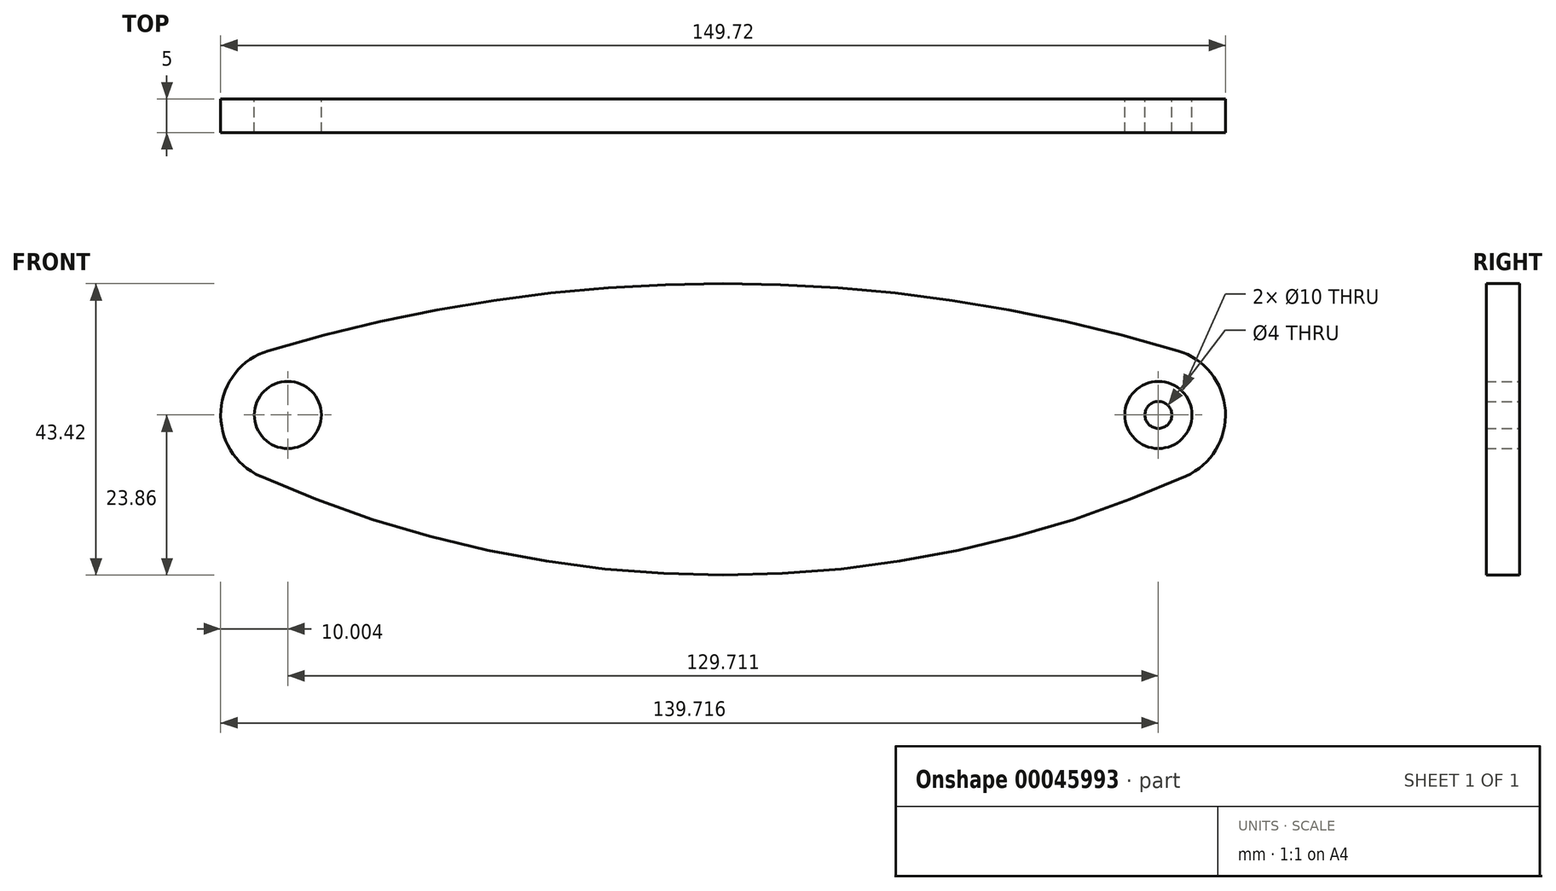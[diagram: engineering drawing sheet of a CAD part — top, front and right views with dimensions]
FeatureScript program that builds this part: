
annotation { "Feature Type Name" : "Feature", "Feature Type Description" : "" }
export const myFeature = defineFeature(function(context is Context, id is Id, definition is map)
    precondition{}
    {
        {
            var Q0;
            Q0=qCreatedBy(makeId("Front.planeOp"),FACE);
            var sketch = newSketch(context, id + "F0", { "sketchPlane" : qUnion([Q0])});
            skLineSegment(sketch, "E0", {"start": v(-64.86, 0) * mm, "end": v(64.86, 0) * mm, "construction": true});
            skCircle(sketch, "E1", {"center": v(-64.86, 0) * mm, "radius": 2 * mm});
            skCircle(sketch, "E2", {"center": v(64.86, 0) * mm, "radius": 2 * mm});
            skCircle(sketch, "E3", {"center": v(-64.86, 0) * mm, "radius": 5 * mm});
            skCircle(sketch, "E4", {"center": v(64.86, 0) * mm, "radius": 5 * mm});
            skArc(sketch, "E5", {"start": v(-68.94, -9.13) * mm, "mid": v(-74.83, 0.64) * mm, "end": v(-67.74, 9.57) * mm});
            skArc(sketch, "E6", {"start": v(68.94, -9.13) * mm, "mid": v(74.83, 0.64) * mm, "end": v(67.74, 9.57) * mm});
            skArc(sketch, "E7", {"start": v(-67.74, 9.57) * mm, "mid": v(0, 19.56) * mm, "end": v(67.74, 9.57) * mm});
            skLineSegment(sketch, "E8", {"start": v(-67.74, 9.57) * mm, "end": v(0, 30) * mm, "construction": true});
            skLineSegment(sketch, "E9", {"start": v(0, 30) * mm, "end": v(67.74, 9.57) * mm, "construction": true});
            skLineSegment(sketch, "E10", {"start": v(68.94, -9.13) * mm, "end": v(0, -40) * mm, "construction": true});
            skLineSegment(sketch, "E11", {"start": v(0, -40) * mm, "end": v(-68.94, -9.13) * mm, "construction": true});
            skArc(sketch, "E12", {"start": v(-68.94, -9.13) * mm, "mid": v(0, -23.86) * mm, "end": v(68.94, -9.13) * mm});
            skSolve(sketch);
        }
        {
            var Q0;
            Q0=makeQuery(id+"F0.imprint","IMPRINT",FACE,{"disambiguationData":[TD([[makeQuery(id+"F0.imprint","IMPRINT",EDGE,{"derivedFrom":sQuery(id+"F0.wireOp",EDGE,"E2")}),-1.0]])]});
            extrude(context, id + "F1", {"entities" : qUnion([Q0]), "depth" : 5 * mm});
        }
        {
            var Q0;
            Q0=makeQuery(id+"F0.imprint","IMPRINT",FACE,{"disambiguationData":[TD([[makeQuery(id+"F0.imprint","IMPRINT",EDGE,{"derivedFrom":sQuery(id+"F0.wireOp",EDGE,"E3")}),-1.0]])]});
            extrude(context, id + "F2", {"entities" : qUnion([Q0]), "depth" : 5 * mm});
        }
    });
